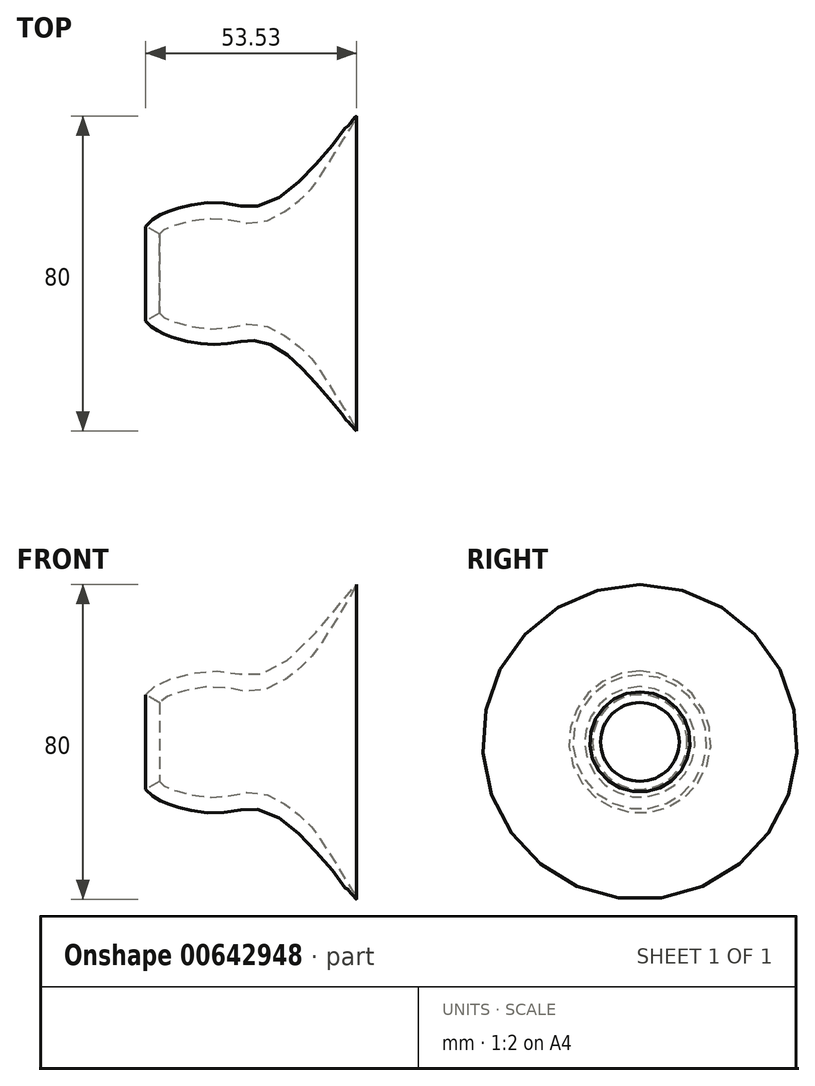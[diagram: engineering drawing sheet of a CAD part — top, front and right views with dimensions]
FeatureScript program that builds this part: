
annotation { "Feature Type Name" : "Feature", "Feature Type Description" : "" }
export const myFeature = defineFeature(function(context is Context, id is Id, definition is map)
    precondition{}
    {
        {
            var Q0;
            Q0=qCreatedBy(makeId("Top.planeOp"),FACE);
            var sketch = newSketch(context, id + "F0", { "sketchPlane" : qUnion([Q0])});
            skLineSegment(sketch, "E0", {"start": v(-33.19, 0) * mm, "end": v(32.56, 0) * mm, "construction": true});
            skFitSpline(sketch, "E1", {"points": [v(-25.81, 12) * mm, v(-21.94, 15) * mm, v(-7.3, 18) * mm, v(7.7, 19) * mm, v(27.7, 40) * mm, v(18.7, 25) * mm, v(14.7, 20) * mm, v(3.7, 13) * mm, v(-7.3, 14) * mm, v(-19.3, 12) * mm, v(-22.35, 10) * mm], "startDerivative": vector(40.78, 53.02) * mm, "endDerivative": vector(-10.53, -45.31) * mm});
            skLineSegment(sketch, "E2", {"start": v(-25.81, 12) * mm, "end": v(-22.35, 10) * mm});
            skSolve(sketch);
        }
        {
            var Q0;
            Q0=makeQuery(id+"F0.imprint","IMPRINT",FACE,{"disambiguationData":[TD([[makeQuery(id+"F0.imprint","IMPRINT",EDGE,{"derivedFrom":sQuery(id+"F0.wireOp",EDGE,"E1")}),-1.0]])]});
            var Q1;
            Q1=sQuery(id+"F0.wireOp",EDGE,"E0");
            revolve(context, id + "F1", {"entities" : qUnion([Q0]), "axis" : qUnion([Q1]), "revolveType" : RevolveType.FULL});
        }
    });
